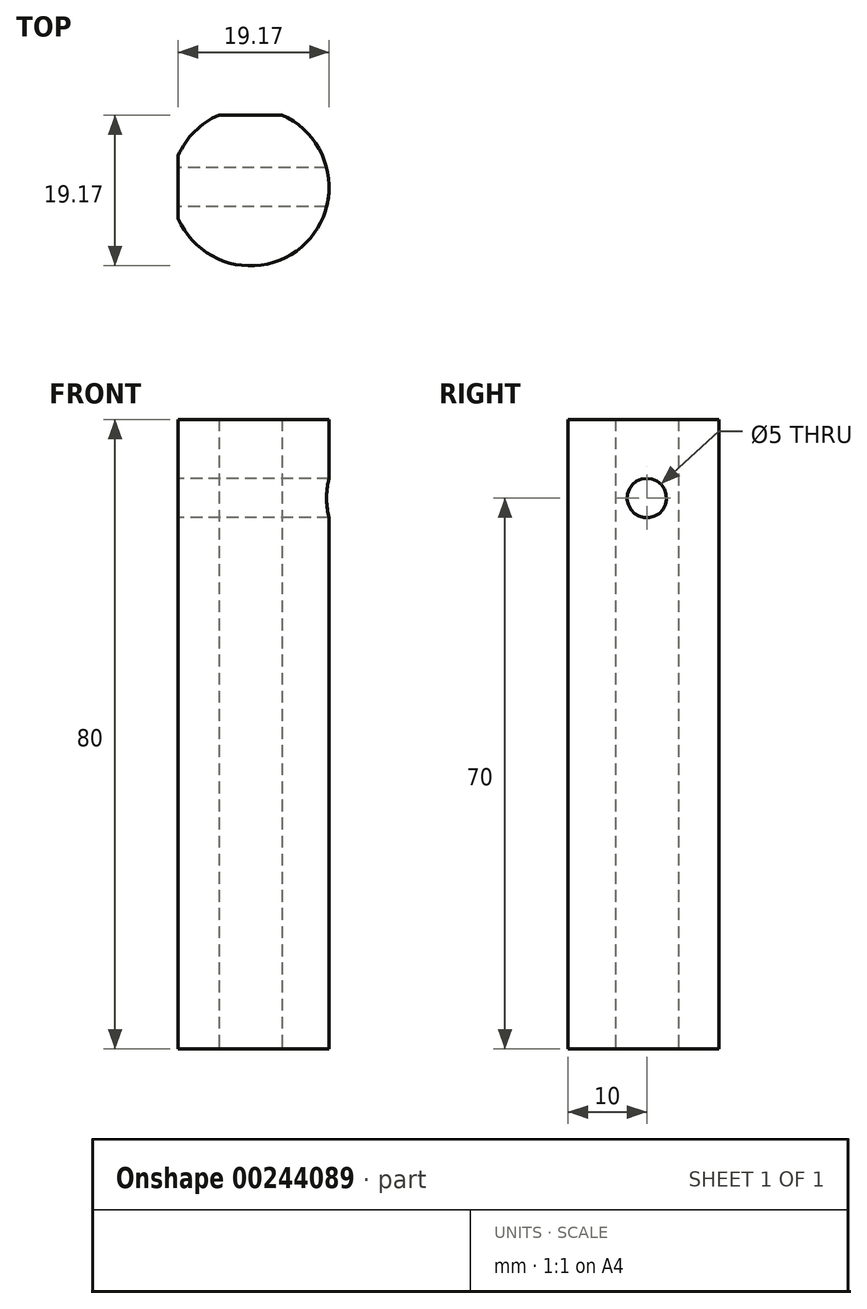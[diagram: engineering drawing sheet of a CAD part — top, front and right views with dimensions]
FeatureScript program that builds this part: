
annotation { "Feature Type Name" : "Feature", "Feature Type Description" : "" }
export const myFeature = defineFeature(function(context is Context, id is Id, definition is map)
    precondition{}
    {
        {
            var Q0;
            Q0=qCreatedBy(makeId("Top.planeOp"),FACE);
            var sketch = newSketch(context, id + "F0", { "sketchPlane" : qUnion([Q0])});
            skArc(sketch, "E0", {"start": v(-9.17, -4) * mm, "mid": v(7.07, -7.07) * mm, "end": v(4, 9.17) * mm});
            skLineSegment(sketch, "E1", {"start": v(-9.17, -4) * mm, "end": v(-9.17, 4) * mm});
            skLineSegment(sketch, "E2", {"start": v(-4, 9.17) * mm, "end": v(4, 9.17) * mm});
            skArc(sketch, "E3.trimOffspring", {"start": v(-4, 9.17) * mm, "mid": v(-7.07, 7.07) * mm, "end": v(-9.17, 4) * mm});
            skSolve(sketch);
        }
        {
            var Q0;
            Q0 = qSketchRegion(id + "F0", true);
            extrude(context, id + "F1", {"entities" : qUnion([Q0]), "depth" : 80 * mm});
        }
        {
            var Q0;
            Q0=makeQuery(id+"F1.opExtrude","SWEPT_FACE",FACE,{"disambiguationData":[OSD([sQuery(id+"F0.wireOp",EDGE,"E1")])]});
            var sketch = newSketch(context, id + "F2", { "sketchPlane" : qUnion([Q0])});
            skPoint(sketch, "E4", {"position": v(0, 70) * mm});
            skSolve(sketch);
        }
        {
            var Q0;
            Q0=sQuery(id+"F2.wireOp",VERTEX,"E4");
            var Q1;
            Q1=makeQuery(id+"F1.opExtrude","SWEPT_BODY",BODY,{"disambiguationData":[OSD([sQuery(id+"F0.wireOp",EDGE,"E0"),sQuery(id+"F0.wireOp",EDGE,"E1"),sQuery(id+"F0.wireOp",EDGE,"E2"),sQuery(id+"F0.wireOp",EDGE,"E3.trimOffspring")])]});
            hole(context, id + "F3", {"style" : HoleStyle.SIMPLE, "endStyle" : HoleEndStyle.THROUGH, "standardTappedOrClearance" : lookupTablePath({ "standard" : "ISO", "engagement" : "75%", "pitch" : "1 mm", "size" : "M6", "type" : "Tapped" }), "standardBlindInLast" : lookupTablePath({ "standard" : "ISO", "engagement" : "75%", "pitch" : "1 mm", "size" : "M6", "type" : "Tapped" }), "holeDiameter" : 5 * mm, "locations" : qUnion([Q0]), "scope" : qUnion([Q1]), "isTappedThrough" : true, "majorDiameter" : 6 * mm, "showTappedDepth" : true});
        }
    });
